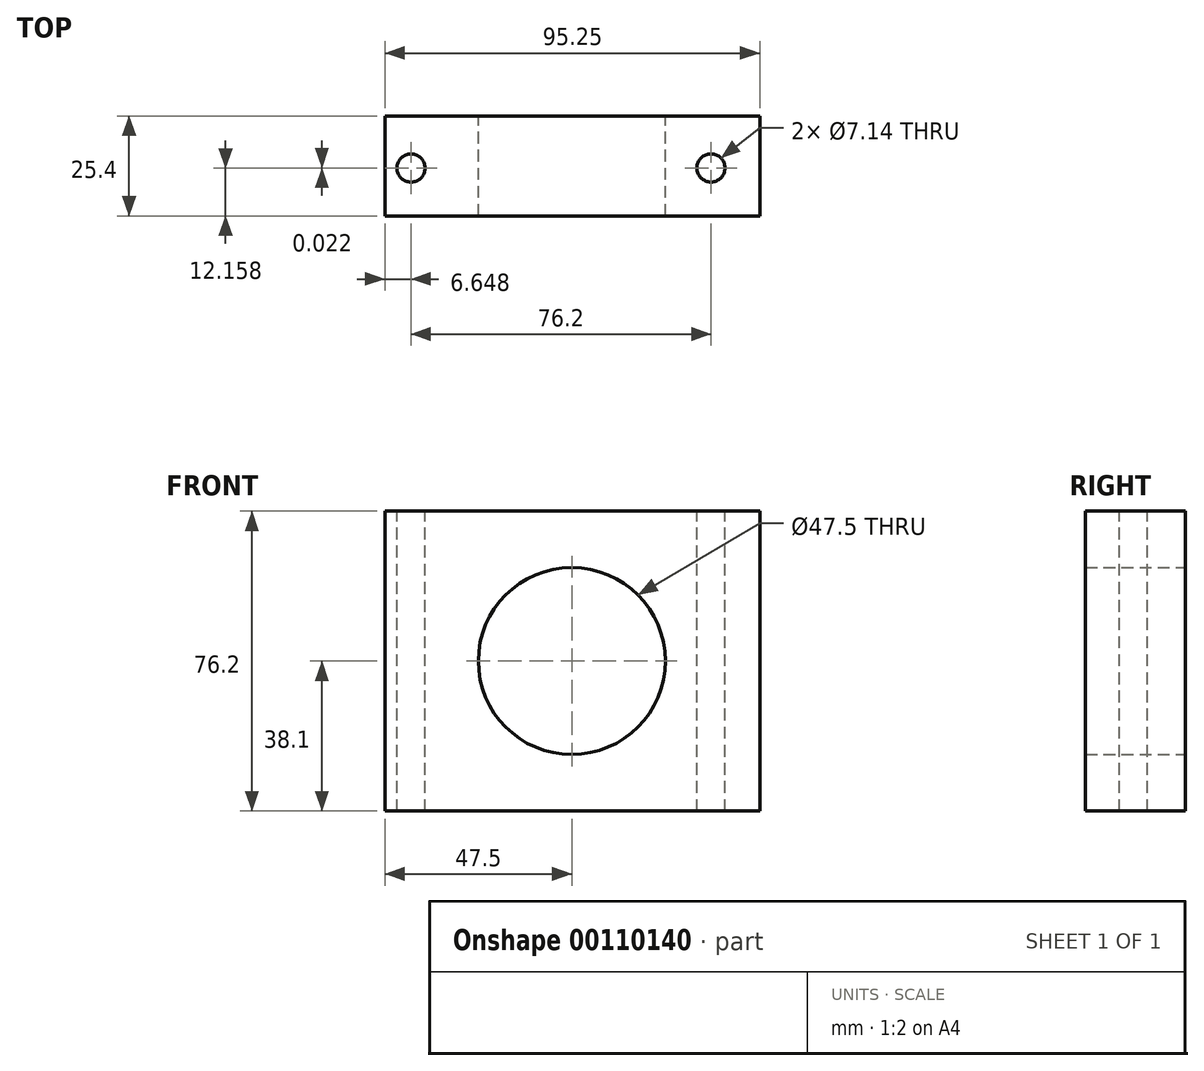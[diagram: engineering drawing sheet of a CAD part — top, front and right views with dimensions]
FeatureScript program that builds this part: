
annotation { "Feature Type Name" : "Feature", "Feature Type Description" : "" }
export const myFeature = defineFeature(function(context is Context, id is Id, definition is map)
    precondition{}
    {
        {
            var Q0;
            Q0=qCreatedBy(makeId("Front.planeOp"),FACE);
            var sketch = newSketch(context, id + "F0", { "sketchPlane" : qUnion([Q0])});
            skLineSegment(sketch, "E0", {"start": v(-47.5, 38.1) * mm, "end": v(-47.5, -38.1) * mm});
            skLineSegment(sketch, "E1", {"start": v(-47.5, -38.1) * mm, "end": v(47.75, -38.1) * mm});
            skLineSegment(sketch, "E2", {"start": v(47.75, -38.1) * mm, "end": v(47.75, 38.1) * mm});
            skLineSegment(sketch, "E3", {"start": v(47.75, 38.1) * mm, "end": v(-47.5, 38.1) * mm});
            skLineSegment(sketch, "E4", {"start": v(47.75, -38.1) * mm, "end": v(47.75, 0) * mm, "construction": true});
            skLineSegment(sketch, "E5", {"start": v(47.75, 0) * mm, "end": v(0, 0) * mm, "construction": true});
            skCircle(sketch, "E6", {"center": v(0, 0) * mm, "radius": 23.75 * mm});
            skSolve(sketch);
        }
        {
            var Q0;
            Q0=makeQuery(id+"F0.imprint","IMPRINT",FACE,{"disambiguationData":[TD([[makeQuery(id+"F0.imprint","IMPRINT",EDGE,{"derivedFrom":sQuery(id+"F0.wireOp",EDGE,"E0")}),1.0]])]});
            extrude(context, id + "F1", {"entities" : qUnion([Q0]), "depth" : 25.4 * mm});
        }
        {
            var Q0;
            Q0=makeQuery(id+"F1.opExtrude","SWEPT_FACE",FACE,{"disambiguationData":[OSD([sQuery(id+"F0.wireOp",EDGE,"E3")])]});
            var sketch = newSketch(context, id + "F2", { "sketchPlane" : qUnion([Q0])});
            skCircle(sketch, "E7", {"center": v(-40.85, -13.24) * mm, "radius": 3.57 * mm});
            skCircle(sketch, "E8", {"center": v(35.35, -13.22) * mm, "radius": 3.57 * mm});
            skSolve(sketch);
        }
        {
            var Q0;
            Q0 = qSketchRegion(id + "F2", true);
            extrude(context, id + "F3", {"entities" : qUnion([Q0]), "operationType" : NewBodyOperationType.REMOVE, "endBound" : BoundingType.THROUGH_ALL, "oppositeDirection" : true, "depth" : 75.73 * mm});
        }
    });
